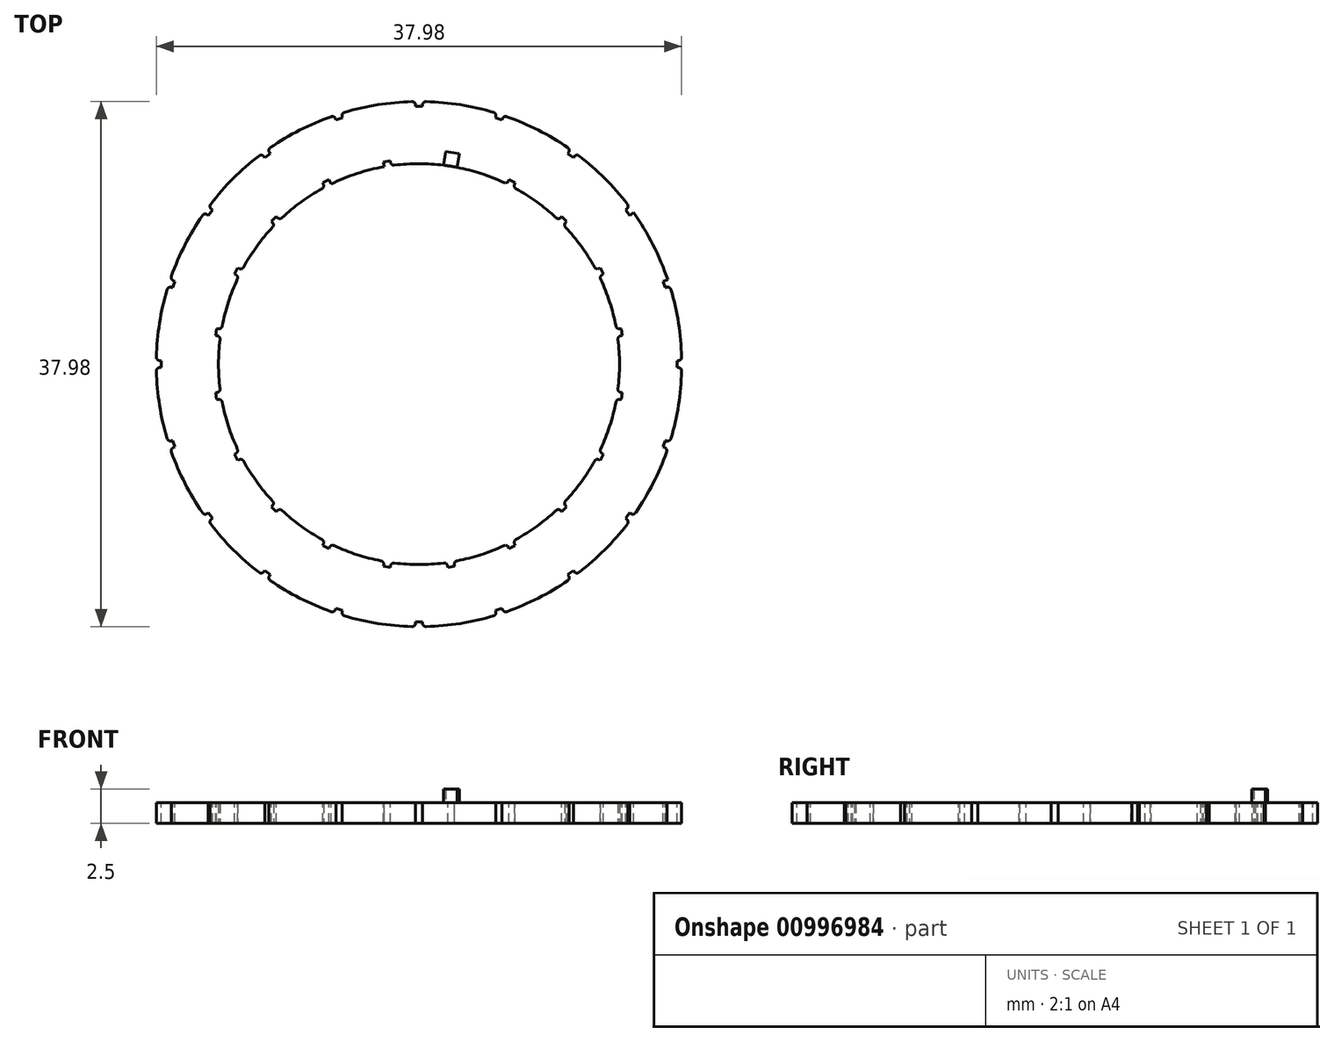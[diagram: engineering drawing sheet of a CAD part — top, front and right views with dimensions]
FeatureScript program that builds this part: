
annotation { "Feature Type Name" : "Feature", "Feature Type Description" : "" }
export const myFeature = defineFeature(function(context is Context, id is Id, definition is map)
    precondition{}
    {
        {
            var Q0;
            Q0=qCreatedBy(makeId("Top.planeOp"),FACE);
            var sketch = newSketch(context, id + "F0", { "sketchPlane" : qUnion([Q0])});
            skCircle(sketch, "E0", {"center": v(0, 0) * mm, "radius": 19 * mm});
            skCircle(sketch, "E1", {"center": v(0, 0) * mm, "radius": 14.5 * mm});
            skSolve(sketch);
        }
        {
            var Q0;
            Q0 = qSketchRegion(id + "F0", true);
            extrude(context, id + "F1", {"entities" : qUnion([Q0]), "depth" : 1.5 * mm, "offsetDistance" : 25 * mm});
        }
        {
            var Q0;
            Q0=makeQuery(id+"F1.opExtrude","CAP_FACE",FACE,{"disambiguationData":[OSD([sQuery(id+"F0.wireOp",EDGE,"E0"),sQuery(id+"F0.wireOp",EDGE,"E1")])],"isStart":false});
            var sketch = newSketch(context, id + "F2", { "sketchPlane" : qUnion([Q0])});
            skLineSegment(sketch, "E2", {"start": v(-0.25, 19) * mm, "end": v(-0.25, 18.65) * mm});
            skLineSegment(sketch, "E3", {"start": v(-0.25, 18.65) * mm, "end": v(0.25, 18.65) * mm});
            skLineSegment(sketch, "E4", {"start": v(0.25, 18.65) * mm, "end": v(0.25, 19) * mm});
            skArc(sketch, "E5", {"start": v(0.25, 19) * mm, "mid": v(0, 19) * mm, "end": v(-0.25, 19) * mm});
            skLineSegment(sketch, "E6.1.0", {"start": v(-6.1, 18) * mm, "end": v(-6, 17.66) * mm});
            skLineSegment(sketch, "E6.1.1", {"start": v(-5.52, 17.81) * mm, "end": v(-5.63, 18.15) * mm});
            skArc(sketch, "E6.1.2", {"start": v(-5.63, 18.15) * mm, "mid": v(-5.87, 18.07) * mm, "end": v(-6.1, 18) * mm});
            skLineSegment(sketch, "E6.1.3", {"start": v(-6, 17.66) * mm, "end": v(-5.52, 17.81) * mm});
            skLineSegment(sketch, "E6.2.0", {"start": v(-11.37, 15.22) * mm, "end": v(-11.16, 14.94) * mm});
            skLineSegment(sketch, "E6.2.1", {"start": v(-10.76, 15.23) * mm, "end": v(-10.96, 15.52) * mm});
            skArc(sketch, "E6.2.2", {"start": v(-10.96, 15.52) * mm, "mid": v(-11.17, 15.37) * mm, "end": v(-11.37, 15.22) * mm});
            skLineSegment(sketch, "E6.2.3", {"start": v(-11.16, 14.94) * mm, "end": v(-10.76, 15.23) * mm});
            skLineSegment(sketch, "E6.3.0", {"start": v(-15.52, 10.96) * mm, "end": v(-15.23, 10.76) * mm});
            skLineSegment(sketch, "E6.3.1", {"start": v(-14.94, 11.16) * mm, "end": v(-15.22, 11.37) * mm});
            skArc(sketch, "E6.3.2", {"start": v(-15.22, 11.37) * mm, "mid": v(-15.37, 11.17) * mm, "end": v(-15.52, 10.96) * mm});
            skLineSegment(sketch, "E6.3.3", {"start": v(-15.23, 10.76) * mm, "end": v(-14.94, 11.16) * mm});
            skLineSegment(sketch, "E6.4.0", {"start": v(-18.15, 5.63) * mm, "end": v(-17.81, 5.52) * mm});
            skLineSegment(sketch, "E6.4.1", {"start": v(-17.66, 6) * mm, "end": v(-18, 6.1) * mm});
            skArc(sketch, "E6.4.2", {"start": v(-18, 6.1) * mm, "mid": v(-18.07, 5.87) * mm, "end": v(-18.15, 5.63) * mm});
            skLineSegment(sketch, "E6.4.3", {"start": v(-17.81, 5.52) * mm, "end": v(-17.66, 6) * mm});
            skLineSegment(sketch, "E6.5.0", {"start": v(-19, -0.25) * mm, "end": v(-18.65, -0.25) * mm});
            skLineSegment(sketch, "E6.5.1", {"start": v(-18.65, 0.25) * mm, "end": v(-19, 0.25) * mm});
            skArc(sketch, "E6.5.2", {"start": v(-19, 0.25) * mm, "mid": v(-19, 0) * mm, "end": v(-19, -0.25) * mm});
            skLineSegment(sketch, "E6.5.3", {"start": v(-18.65, -0.25) * mm, "end": v(-18.65, 0.25) * mm});
            skLineSegment(sketch, "E6.6.0", {"start": v(-18, -6.1) * mm, "end": v(-17.66, -6) * mm});
            skLineSegment(sketch, "E6.6.1", {"start": v(-17.81, -5.52) * mm, "end": v(-18.15, -5.63) * mm});
            skArc(sketch, "E6.6.2", {"start": v(-18.15, -5.63) * mm, "mid": v(-18.07, -5.87) * mm, "end": v(-18, -6.1) * mm});
            skLineSegment(sketch, "E6.6.3", {"start": v(-17.66, -6) * mm, "end": v(-17.81, -5.52) * mm});
            skLineSegment(sketch, "E6.7.0", {"start": v(-15.22, -11.37) * mm, "end": v(-14.94, -11.16) * mm});
            skLineSegment(sketch, "E6.7.1", {"start": v(-15.23, -10.76) * mm, "end": v(-15.52, -10.96) * mm});
            skArc(sketch, "E6.7.2", {"start": v(-15.52, -10.96) * mm, "mid": v(-15.37, -11.17) * mm, "end": v(-15.22, -11.37) * mm});
            skLineSegment(sketch, "E6.7.3", {"start": v(-14.94, -11.16) * mm, "end": v(-15.23, -10.76) * mm});
            skLineSegment(sketch, "E6.8.0", {"start": v(-10.96, -15.52) * mm, "end": v(-10.76, -15.23) * mm});
            skLineSegment(sketch, "E6.8.1", {"start": v(-11.16, -14.94) * mm, "end": v(-11.37, -15.22) * mm});
            skArc(sketch, "E6.8.2", {"start": v(-11.37, -15.22) * mm, "mid": v(-11.17, -15.37) * mm, "end": v(-10.96, -15.52) * mm});
            skLineSegment(sketch, "E6.8.3", {"start": v(-10.76, -15.23) * mm, "end": v(-11.16, -14.94) * mm});
            skLineSegment(sketch, "E6.9.0", {"start": v(-5.63, -18.15) * mm, "end": v(-5.52, -17.81) * mm});
            skLineSegment(sketch, "E6.9.1", {"start": v(-6, -17.66) * mm, "end": v(-6.1, -18) * mm});
            skArc(sketch, "E6.9.2", {"start": v(-6.1, -18) * mm, "mid": v(-5.87, -18.07) * mm, "end": v(-5.63, -18.15) * mm});
            skLineSegment(sketch, "E6.9.3", {"start": v(-5.52, -17.81) * mm, "end": v(-6, -17.66) * mm});
            skLineSegment(sketch, "E6.10.0", {"start": v(0.25, -19) * mm, "end": v(0.25, -18.65) * mm});
            skLineSegment(sketch, "E6.10.1", {"start": v(-0.25, -18.65) * mm, "end": v(-0.25, -19) * mm});
            skArc(sketch, "E6.10.2", {"start": v(-0.25, -19) * mm, "mid": v(0, -19) * mm, "end": v(0.25, -19) * mm});
            skLineSegment(sketch, "E6.10.3", {"start": v(0.25, -18.65) * mm, "end": v(-0.25, -18.65) * mm});
            skLineSegment(sketch, "E6.11.0", {"start": v(6.1, -18) * mm, "end": v(6, -17.66) * mm});
            skLineSegment(sketch, "E6.11.1", {"start": v(5.52, -17.81) * mm, "end": v(5.63, -18.15) * mm});
            skArc(sketch, "E6.11.2", {"start": v(5.63, -18.15) * mm, "mid": v(5.87, -18.07) * mm, "end": v(6.1, -18) * mm});
            skLineSegment(sketch, "E6.11.3", {"start": v(6, -17.66) * mm, "end": v(5.52, -17.81) * mm});
            skLineSegment(sketch, "E6.12.0", {"start": v(11.37, -15.22) * mm, "end": v(11.16, -14.94) * mm});
            skLineSegment(sketch, "E6.12.1", {"start": v(10.76, -15.23) * mm, "end": v(10.96, -15.52) * mm});
            skArc(sketch, "E6.12.2", {"start": v(10.96, -15.52) * mm, "mid": v(11.17, -15.37) * mm, "end": v(11.37, -15.22) * mm});
            skLineSegment(sketch, "E6.12.3", {"start": v(11.16, -14.94) * mm, "end": v(10.76, -15.23) * mm});
            skLineSegment(sketch, "E6.13.0", {"start": v(15.52, -10.96) * mm, "end": v(15.23, -10.76) * mm});
            skLineSegment(sketch, "E6.13.1", {"start": v(14.94, -11.16) * mm, "end": v(15.22, -11.37) * mm});
            skArc(sketch, "E6.13.2", {"start": v(15.22, -11.37) * mm, "mid": v(15.37, -11.17) * mm, "end": v(15.52, -10.96) * mm});
            skLineSegment(sketch, "E6.13.3", {"start": v(15.23, -10.76) * mm, "end": v(14.94, -11.16) * mm});
            skLineSegment(sketch, "E6.14.0", {"start": v(18.15, -5.63) * mm, "end": v(17.81, -5.52) * mm});
            skLineSegment(sketch, "E6.14.1", {"start": v(17.66, -6) * mm, "end": v(18, -6.1) * mm});
            skArc(sketch, "E6.14.2", {"start": v(18, -6.1) * mm, "mid": v(18.07, -5.87) * mm, "end": v(18.15, -5.63) * mm});
            skLineSegment(sketch, "E6.14.3", {"start": v(17.81, -5.52) * mm, "end": v(17.66, -6) * mm});
            skLineSegment(sketch, "E6.15.0", {"start": v(19, 0.25) * mm, "end": v(18.65, 0.25) * mm});
            skLineSegment(sketch, "E6.15.1", {"start": v(18.65, -0.25) * mm, "end": v(19, -0.25) * mm});
            skArc(sketch, "E6.15.2", {"start": v(19, -0.25) * mm, "mid": v(19, 0) * mm, "end": v(19, 0.25) * mm});
            skLineSegment(sketch, "E6.15.3", {"start": v(18.65, 0.25) * mm, "end": v(18.65, -0.25) * mm});
            skLineSegment(sketch, "E6.16.0", {"start": v(18, 6.1) * mm, "end": v(17.66, 6) * mm});
            skLineSegment(sketch, "E6.16.1", {"start": v(17.81, 5.52) * mm, "end": v(18.15, 5.63) * mm});
            skArc(sketch, "E6.16.2", {"start": v(18.15, 5.63) * mm, "mid": v(18.07, 5.87) * mm, "end": v(18, 6.1) * mm});
            skLineSegment(sketch, "E6.16.3", {"start": v(17.66, 6) * mm, "end": v(17.81, 5.52) * mm});
            skLineSegment(sketch, "E6.17.0", {"start": v(15.22, 11.37) * mm, "end": v(14.94, 11.16) * mm});
            skLineSegment(sketch, "E6.17.1", {"start": v(15.23, 10.76) * mm, "end": v(15.52, 10.96) * mm});
            skArc(sketch, "E6.17.2", {"start": v(15.52, 10.96) * mm, "mid": v(15.37, 11.17) * mm, "end": v(15.22, 11.37) * mm});
            skLineSegment(sketch, "E6.17.3", {"start": v(14.94, 11.16) * mm, "end": v(15.23, 10.76) * mm});
            skLineSegment(sketch, "E6.18.0", {"start": v(10.96, 15.52) * mm, "end": v(10.76, 15.23) * mm});
            skLineSegment(sketch, "E6.18.1", {"start": v(11.16, 14.94) * mm, "end": v(11.37, 15.22) * mm});
            skArc(sketch, "E6.18.2", {"start": v(11.37, 15.22) * mm, "mid": v(11.17, 15.37) * mm, "end": v(10.96, 15.52) * mm});
            skLineSegment(sketch, "E6.18.3", {"start": v(10.76, 15.23) * mm, "end": v(11.16, 14.94) * mm});
            skLineSegment(sketch, "E6.19.0", {"start": v(5.63, 18.15) * mm, "end": v(5.52, 17.81) * mm});
            skLineSegment(sketch, "E6.19.1", {"start": v(6, 17.66) * mm, "end": v(6.1, 18) * mm});
            skArc(sketch, "E6.19.2", {"start": v(6.1, 18) * mm, "mid": v(5.87, 18.07) * mm, "end": v(5.63, 18.15) * mm});
            skLineSegment(sketch, "E6.19.3", {"start": v(5.52, 17.81) * mm, "end": v(6, 17.66) * mm});
            skSolve(sketch);
        }
        {
            var Q0;
            Q0 = qSketchRegion(id + "F2", true);
            extrude(context, id + "F3", {"entities" : qUnion([Q0]), "operationType" : NewBodyOperationType.REMOVE, "endBound" : BoundingType.THROUGH_ALL, "oppositeDirection" : true, "depth" : 25 * mm, "offsetDistance" : 25 * mm});
        }
        {
            var Q0;
            Q0=makeQuery(id+"F1.opExtrude","CAP_FACE",FACE,{"disambiguationData":[OSD([sQuery(id+"F0.wireOp",EDGE,"E0"),sQuery(id+"F0.wireOp",EDGE,"E1")])],"isStart":false});
            var sketch = newSketch(context, id + "F4", { "sketchPlane" : qUnion([Q0])});
            skLineSegment(sketch, "E7", {"start": v(0, 0) * mm, "end": v(-2.5, 15.78) * mm, "construction": true});
            skLineSegment(sketch, "E8", {"start": v(-2.51, 14.28) * mm, "end": v(-2.57, 14.63) * mm});
            skLineSegment(sketch, "E9", {"start": v(-2.57, 14.63) * mm, "end": v(-2.08, 14.7) * mm});
            skLineSegment(sketch, "E10", {"start": v(-2.08, 14.7) * mm, "end": v(-2.02, 14.36) * mm});
            skArc(sketch, "E11", {"start": v(-2.02, 14.36) * mm, "mid": v(-2.27, 14.32) * mm, "end": v(-2.51, 14.28) * mm});
            skLineSegment(sketch, "E12.1.0", {"start": v(-6.8, 12.8) * mm, "end": v(-6.96, 13.12) * mm});
            skLineSegment(sketch, "E12.1.1", {"start": v(-6.52, 13.34) * mm, "end": v(-6.36, 13.03) * mm});
            skLineSegment(sketch, "E12.1.2", {"start": v(-6.96, 13.12) * mm, "end": v(-6.52, 13.34) * mm});
            skArc(sketch, "E12.1.3", {"start": v(-6.36, 13.03) * mm, "mid": v(-6.58, 12.92) * mm, "end": v(-6.8, 12.8) * mm});
            skLineSegment(sketch, "E12.2.0", {"start": v(-10.43, 10.07) * mm, "end": v(-10.68, 10.32) * mm});
            skLineSegment(sketch, "E12.2.1", {"start": v(-10.32, 10.68) * mm, "end": v(-10.07, 10.43) * mm});
            skLineSegment(sketch, "E12.2.2", {"start": v(-10.68, 10.32) * mm, "end": v(-10.32, 10.68) * mm});
            skArc(sketch, "E12.2.3", {"start": v(-10.07, 10.43) * mm, "mid": v(-10.25, 10.25) * mm, "end": v(-10.43, 10.07) * mm});
            skLineSegment(sketch, "E12.3.0", {"start": v(-13.03, 6.36) * mm, "end": v(-13.34, 6.52) * mm});
            skLineSegment(sketch, "E12.3.1", {"start": v(-13.12, 6.96) * mm, "end": v(-12.8, 6.8) * mm});
            skLineSegment(sketch, "E12.3.2", {"start": v(-13.34, 6.52) * mm, "end": v(-13.12, 6.96) * mm});
            skArc(sketch, "E12.3.3", {"start": v(-12.8, 6.8) * mm, "mid": v(-12.92, 6.58) * mm, "end": v(-13.03, 6.36) * mm});
            skLineSegment(sketch, "E12.4.0", {"start": v(-14.36, 2.02) * mm, "end": v(-14.7, 2.08) * mm});
            skLineSegment(sketch, "E12.4.1", {"start": v(-14.63, 2.57) * mm, "end": v(-14.28, 2.51) * mm});
            skLineSegment(sketch, "E12.4.2", {"start": v(-14.7, 2.08) * mm, "end": v(-14.63, 2.57) * mm});
            skArc(sketch, "E12.4.3", {"start": v(-14.28, 2.51) * mm, "mid": v(-14.32, 2.27) * mm, "end": v(-14.36, 2.02) * mm});
            skLineSegment(sketch, "E12.5.0", {"start": v(-14.28, -2.51) * mm, "end": v(-14.63, -2.57) * mm});
            skLineSegment(sketch, "E12.5.1", {"start": v(-14.7, -2.08) * mm, "end": v(-14.36, -2.02) * mm});
            skLineSegment(sketch, "E12.5.2", {"start": v(-14.63, -2.57) * mm, "end": v(-14.7, -2.08) * mm});
            skArc(sketch, "E12.5.3", {"start": v(-14.36, -2.02) * mm, "mid": v(-14.32, -2.27) * mm, "end": v(-14.28, -2.51) * mm});
            skLineSegment(sketch, "E12.6.0", {"start": v(-12.8, -6.8) * mm, "end": v(-13.12, -6.96) * mm});
            skLineSegment(sketch, "E12.6.1", {"start": v(-13.34, -6.52) * mm, "end": v(-13.03, -6.36) * mm});
            skLineSegment(sketch, "E12.6.2", {"start": v(-13.12, -6.96) * mm, "end": v(-13.34, -6.52) * mm});
            skArc(sketch, "E12.6.3", {"start": v(-13.03, -6.36) * mm, "mid": v(-12.92, -6.58) * mm, "end": v(-12.8, -6.8) * mm});
            skLineSegment(sketch, "E12.7.0", {"start": v(-10.07, -10.43) * mm, "end": v(-10.32, -10.68) * mm});
            skLineSegment(sketch, "E12.7.1", {"start": v(-10.68, -10.32) * mm, "end": v(-10.43, -10.07) * mm});
            skLineSegment(sketch, "E12.7.2", {"start": v(-10.32, -10.68) * mm, "end": v(-10.68, -10.32) * mm});
            skArc(sketch, "E12.7.3", {"start": v(-10.43, -10.07) * mm, "mid": v(-10.25, -10.25) * mm, "end": v(-10.07, -10.43) * mm});
            skLineSegment(sketch, "E12.8.0", {"start": v(-6.36, -13.03) * mm, "end": v(-6.52, -13.34) * mm});
            skLineSegment(sketch, "E12.8.1", {"start": v(-6.96, -13.12) * mm, "end": v(-6.8, -12.8) * mm});
            skLineSegment(sketch, "E12.8.2", {"start": v(-6.52, -13.34) * mm, "end": v(-6.96, -13.12) * mm});
            skArc(sketch, "E12.8.3", {"start": v(-6.8, -12.8) * mm, "mid": v(-6.58, -12.92) * mm, "end": v(-6.36, -13.03) * mm});
            skLineSegment(sketch, "E12.9.0", {"start": v(-2.02, -14.36) * mm, "end": v(-2.08, -14.7) * mm});
            skLineSegment(sketch, "E12.9.1", {"start": v(-2.57, -14.63) * mm, "end": v(-2.51, -14.28) * mm});
            skLineSegment(sketch, "E12.9.2", {"start": v(-2.08, -14.7) * mm, "end": v(-2.57, -14.63) * mm});
            skArc(sketch, "E12.9.3", {"start": v(-2.51, -14.28) * mm, "mid": v(-2.27, -14.32) * mm, "end": v(-2.02, -14.36) * mm});
            skLineSegment(sketch, "E12.10.0", {"start": v(2.51, -14.28) * mm, "end": v(2.57, -14.63) * mm});
            skLineSegment(sketch, "E12.10.1", {"start": v(2.08, -14.7) * mm, "end": v(2.02, -14.36) * mm});
            skLineSegment(sketch, "E12.10.2", {"start": v(2.57, -14.63) * mm, "end": v(2.08, -14.7) * mm});
            skArc(sketch, "E12.10.3", {"start": v(2.02, -14.36) * mm, "mid": v(2.27, -14.32) * mm, "end": v(2.51, -14.28) * mm});
            skLineSegment(sketch, "E12.11.0", {"start": v(6.8, -12.8) * mm, "end": v(6.96, -13.12) * mm});
            skLineSegment(sketch, "E12.11.1", {"start": v(6.52, -13.34) * mm, "end": v(6.36, -13.03) * mm});
            skLineSegment(sketch, "E12.11.2", {"start": v(6.96, -13.12) * mm, "end": v(6.52, -13.34) * mm});
            skArc(sketch, "E12.11.3", {"start": v(6.36, -13.03) * mm, "mid": v(6.58, -12.92) * mm, "end": v(6.8, -12.8) * mm});
            skLineSegment(sketch, "E12.12.0", {"start": v(10.43, -10.07) * mm, "end": v(10.68, -10.32) * mm});
            skLineSegment(sketch, "E12.12.1", {"start": v(10.32, -10.68) * mm, "end": v(10.07, -10.43) * mm});
            skLineSegment(sketch, "E12.12.2", {"start": v(10.68, -10.32) * mm, "end": v(10.32, -10.68) * mm});
            skArc(sketch, "E12.12.3", {"start": v(10.07, -10.43) * mm, "mid": v(10.25, -10.25) * mm, "end": v(10.43, -10.07) * mm});
            skLineSegment(sketch, "E12.13.0", {"start": v(13.03, -6.36) * mm, "end": v(13.34, -6.52) * mm});
            skLineSegment(sketch, "E12.13.1", {"start": v(13.12, -6.96) * mm, "end": v(12.8, -6.8) * mm});
            skLineSegment(sketch, "E12.13.2", {"start": v(13.34, -6.52) * mm, "end": v(13.12, -6.96) * mm});
            skArc(sketch, "E12.13.3", {"start": v(12.8, -6.8) * mm, "mid": v(12.92, -6.58) * mm, "end": v(13.03, -6.36) * mm});
            skLineSegment(sketch, "E12.14.0", {"start": v(14.36, -2.02) * mm, "end": v(14.7, -2.08) * mm});
            skLineSegment(sketch, "E12.14.1", {"start": v(14.63, -2.57) * mm, "end": v(14.28, -2.51) * mm});
            skLineSegment(sketch, "E12.14.2", {"start": v(14.7, -2.08) * mm, "end": v(14.63, -2.57) * mm});
            skArc(sketch, "E12.14.3", {"start": v(14.28, -2.51) * mm, "mid": v(14.32, -2.27) * mm, "end": v(14.36, -2.02) * mm});
            skLineSegment(sketch, "E12.15.0", {"start": v(14.28, 2.51) * mm, "end": v(14.63, 2.57) * mm});
            skLineSegment(sketch, "E12.15.1", {"start": v(14.7, 2.08) * mm, "end": v(14.36, 2.02) * mm});
            skLineSegment(sketch, "E12.15.2", {"start": v(14.63, 2.57) * mm, "end": v(14.7, 2.08) * mm});
            skArc(sketch, "E12.15.3", {"start": v(14.36, 2.02) * mm, "mid": v(14.32, 2.27) * mm, "end": v(14.28, 2.51) * mm});
            skLineSegment(sketch, "E12.16.0", {"start": v(12.8, 6.8) * mm, "end": v(13.12, 6.96) * mm});
            skLineSegment(sketch, "E12.16.1", {"start": v(13.34, 6.52) * mm, "end": v(13.03, 6.36) * mm});
            skLineSegment(sketch, "E12.16.2", {"start": v(13.12, 6.96) * mm, "end": v(13.34, 6.52) * mm});
            skArc(sketch, "E12.16.3", {"start": v(13.03, 6.36) * mm, "mid": v(12.92, 6.58) * mm, "end": v(12.8, 6.8) * mm});
            skLineSegment(sketch, "E12.17.0", {"start": v(10.07, 10.43) * mm, "end": v(10.32, 10.68) * mm});
            skLineSegment(sketch, "E12.17.1", {"start": v(10.68, 10.32) * mm, "end": v(10.43, 10.07) * mm});
            skLineSegment(sketch, "E12.17.2", {"start": v(10.32, 10.68) * mm, "end": v(10.68, 10.32) * mm});
            skArc(sketch, "E12.17.3", {"start": v(10.43, 10.07) * mm, "mid": v(10.25, 10.25) * mm, "end": v(10.07, 10.43) * mm});
            skLineSegment(sketch, "E12.18.0", {"start": v(6.36, 13.03) * mm, "end": v(6.52, 13.34) * mm});
            skLineSegment(sketch, "E12.18.1", {"start": v(6.96, 13.12) * mm, "end": v(6.8, 12.8) * mm});
            skLineSegment(sketch, "E12.18.2", {"start": v(6.52, 13.34) * mm, "end": v(6.96, 13.12) * mm});
            skArc(sketch, "E12.18.3", {"start": v(6.8, 12.8) * mm, "mid": v(6.58, 12.92) * mm, "end": v(6.36, 13.03) * mm});
            skLineSegment(sketch, "E12.19.0", {"start": v(2.02, 14.36) * mm, "end": v(2.08, 14.7) * mm});
            skLineSegment(sketch, "E12.19.1", {"start": v(2.57, 14.63) * mm, "end": v(2.51, 14.28) * mm});
            skLineSegment(sketch, "E12.19.2", {"start": v(2.08, 14.7) * mm, "end": v(2.57, 14.63) * mm});
            skArc(sketch, "E12.19.3", {"start": v(2.51, 14.28) * mm, "mid": v(2.27, 14.32) * mm, "end": v(2.02, 14.36) * mm});
            skSolve(sketch);
        }
        {
            var Q0;
            Q0 = qSketchRegion(id + "F4", true);
            extrude(context, id + "F5", {"entities" : qUnion([Q0]), "operationType" : NewBodyOperationType.REMOVE, "endBound" : BoundingType.THROUGH_ALL, "oppositeDirection" : true, "depth" : 25 * mm, "offsetDistance" : 25 * mm});
        }
        {
            var Q0;
            Q0=makeQuery(id+"F1.opExtrude","CAP_FACE",FACE,{"disambiguationData":[OSD([sQuery(id+"F0.wireOp",EDGE,"E0"),sQuery(id+"F0.wireOp",EDGE,"E1")])],"isStart":true});
            var sketch = newSketch(context, id + "F6", { "sketchPlane" : qUnion([Q0])});
            skLineSegment(sketch, "E13", {"start": v(2.51, -14.28) * mm, "end": v(2.57, -14.63) * mm});
            skLineSegment(sketch, "E14", {"start": v(2.57, -14.63) * mm, "end": v(2.08, -14.7) * mm});
            skLineSegment(sketch, "E15", {"start": v(2.08, -14.7) * mm, "end": v(2.02, -14.36) * mm});
            skArc(sketch, "E16", {"start": v(2.02, -14.36) * mm, "mid": v(2.27, -14.32) * mm, "end": v(2.51, -14.28) * mm});
            skSolve(sketch);
        }
        {
            var Q0;
            Q0 = qSketchRegion(id + "F6", true);
            extrude(context, id + "F7", {"entities" : qUnion([Q0]), "operationType" : NewBodyOperationType.ADD, "oppositeDirection" : true, "depth" : 2.5 * mm, "offsetDistance" : 25 * mm});
        }
        {
            var Q0;
            Q0=makeQuery(id+"F1.opExtrude","CAP_FACE",FACE,{"disambiguationData":[OSD([sQuery(id+"F0.wireOp",EDGE,"E0"),sQuery(id+"F0.wireOp",EDGE,"E1")])],"isStart":false});
            var sketch = newSketch(context, id + "F8", { "sketchPlane" : qUnion([Q0])});
            skLineSegment(sketch, "E17", {"start": v(1.77, 14.4) * mm, "end": v(1.93, 15.38) * mm});
            skLineSegment(sketch, "E18", {"start": v(1.93, 15.38) * mm, "end": v(2.92, 15.22) * mm});
            skLineSegment(sketch, "E19", {"start": v(2.92, 15.22) * mm, "end": v(2.76, 14.23) * mm});
            skArc(sketch, "E20", {"start": v(2.76, 14.23) * mm, "mid": v(2.27, 14.32) * mm, "end": v(1.77, 14.4) * mm});
            skSolve(sketch);
        }
        {
            var Q0;
            Q0 = qSketchRegion(id + "F8", true);
            var Q1;
            Q1=makeQuery(id+"F7.opExtrude","CAP_FACE",FACE,{"disambiguationData":[OSD([sQuery(id+"F6.wireOp",EDGE,"E13"),sQuery(id+"F6.wireOp",EDGE,"E14"),sQuery(id+"F6.wireOp",EDGE,"E15"),sQuery(id+"F6.wireOp",EDGE,"E16")])],"isStart":false});
            extrude(context, id + "F9", {"entities" : qUnion([Q0]), "operationType" : NewBodyOperationType.ADD, "endBound" : BoundingType.UP_TO_SURFACE, "depth" : 25 * mm, "endBoundEntityFace" : qUnion([Q1]), "offsetDistance" : 25 * mm});
        }
        {
            var Q0;
            Q0=makeQuery(id+"F3.boolean.opBoolean","COPY",EDGE,{"derivedFrom":makeQuery(id+"F3.opExtrude","SWEPT_EDGE",EDGE,{"disambiguationData":[OSD([sQuery(id+"F0.wireOp",EDGE,"E0"),sQuery(id+"F2.wireOp",EDGE,"E6.19.1"),sQuery(id+"F2.wireOp",EDGE,"E6.19.2")])]})});
            var Q1;
            Q1=makeQuery(id+"F3.boolean.opBoolean","COPY",EDGE,{"derivedFrom":makeQuery(id+"F3.opExtrude","SWEPT_EDGE",EDGE,{"disambiguationData":[OSD([sQuery(id+"F0.wireOp",EDGE,"E0"),sQuery(id+"F2.wireOp",EDGE,"E6.19.0"),sQuery(id+"F2.wireOp",EDGE,"E6.19.2")])]})});
            var Q2;
            Q2=makeQuery(id+"F3.boolean.opBoolean","COPY",EDGE,{"derivedFrom":makeQuery(id+"F3.opExtrude","SWEPT_EDGE",EDGE,{"disambiguationData":[OSD([sQuery(id+"F0.wireOp",EDGE,"E0"),sQuery(id+"F2.wireOp",EDGE,"E4"),sQuery(id+"F2.wireOp",EDGE,"E5")])]})});
            var Q3;
            Q3=makeQuery(id+"F3.boolean.opBoolean","COPY",EDGE,{"derivedFrom":makeQuery(id+"F3.opExtrude","SWEPT_EDGE",EDGE,{"disambiguationData":[OSD([sQuery(id+"F0.wireOp",EDGE,"E0"),sQuery(id+"F2.wireOp",EDGE,"E2"),sQuery(id+"F2.wireOp",EDGE,"E5")])]})});
            var Q4;
            Q4=makeQuery(id+"F3.boolean.opBoolean","COPY",EDGE,{"derivedFrom":makeQuery(id+"F3.opExtrude","SWEPT_EDGE",EDGE,{"disambiguationData":[OSD([sQuery(id+"F0.wireOp",EDGE,"E0"),sQuery(id+"F2.wireOp",EDGE,"E6.1.1"),sQuery(id+"F2.wireOp",EDGE,"E6.1.2")])]})});
            var Q5;
            Q5=makeQuery(id+"F3.boolean.opBoolean","COPY",EDGE,{"derivedFrom":makeQuery(id+"F3.opExtrude","SWEPT_EDGE",EDGE,{"disambiguationData":[OSD([sQuery(id+"F0.wireOp",EDGE,"E0"),sQuery(id+"F2.wireOp",EDGE,"E6.1.0"),sQuery(id+"F2.wireOp",EDGE,"E6.1.2")])]})});
            var Q6;
            Q6=makeQuery(id+"F3.boolean.opBoolean","COPY",EDGE,{"derivedFrom":makeQuery(id+"F3.opExtrude","SWEPT_EDGE",EDGE,{"disambiguationData":[OSD([sQuery(id+"F0.wireOp",EDGE,"E0"),sQuery(id+"F2.wireOp",EDGE,"E6.18.0"),sQuery(id+"F2.wireOp",EDGE,"E6.18.2")])]})});
            var Q7;
            Q7=makeQuery(id+"F3.boolean.opBoolean","COPY",EDGE,{"derivedFrom":makeQuery(id+"F3.opExtrude","SWEPT_EDGE",EDGE,{"disambiguationData":[OSD([sQuery(id+"F0.wireOp",EDGE,"E0"),sQuery(id+"F2.wireOp",EDGE,"E6.18.1"),sQuery(id+"F2.wireOp",EDGE,"E6.18.2")])]})});
            var Q8;
            Q8=makeQuery(id+"F3.boolean.opBoolean","COPY",EDGE,{"derivedFrom":makeQuery(id+"F3.opExtrude","SWEPT_EDGE",EDGE,{"disambiguationData":[OSD([sQuery(id+"F0.wireOp",EDGE,"E0"),sQuery(id+"F2.wireOp",EDGE,"E6.17.0"),sQuery(id+"F2.wireOp",EDGE,"E6.17.2")])]})});
            var Q9;
            Q9=makeQuery(id+"F3.boolean.opBoolean","COPY",EDGE,{"derivedFrom":makeQuery(id+"F3.opExtrude","SWEPT_EDGE",EDGE,{"disambiguationData":[OSD([sQuery(id+"F0.wireOp",EDGE,"E0"),sQuery(id+"F2.wireOp",EDGE,"E6.17.1"),sQuery(id+"F2.wireOp",EDGE,"E6.17.2")])]})});
            var Q10;
            Q10=makeQuery(id+"F3.boolean.opBoolean","COPY",EDGE,{"derivedFrom":makeQuery(id+"F3.opExtrude","SWEPT_EDGE",EDGE,{"disambiguationData":[OSD([sQuery(id+"F0.wireOp",EDGE,"E0"),sQuery(id+"F2.wireOp",EDGE,"E6.16.0"),sQuery(id+"F2.wireOp",EDGE,"E6.16.2")])]})});
            var Q11;
            Q11=makeQuery(id+"F3.boolean.opBoolean","COPY",EDGE,{"derivedFrom":makeQuery(id+"F3.opExtrude","SWEPT_EDGE",EDGE,{"disambiguationData":[OSD([sQuery(id+"F0.wireOp",EDGE,"E0"),sQuery(id+"F2.wireOp",EDGE,"E6.16.1"),sQuery(id+"F2.wireOp",EDGE,"E6.16.2")])]})});
            var Q12;
            Q12=makeQuery(id+"F3.boolean.opBoolean","COPY",EDGE,{"derivedFrom":makeQuery(id+"F3.opExtrude","SWEPT_EDGE",EDGE,{"disambiguationData":[OSD([sQuery(id+"F0.wireOp",EDGE,"E0"),sQuery(id+"F2.wireOp",EDGE,"E6.15.0"),sQuery(id+"F2.wireOp",EDGE,"E6.15.2")])]})});
            var Q13;
            Q13=makeQuery(id+"F3.boolean.opBoolean","COPY",EDGE,{"derivedFrom":makeQuery(id+"F3.opExtrude","SWEPT_EDGE",EDGE,{"disambiguationData":[OSD([sQuery(id+"F0.wireOp",EDGE,"E0"),sQuery(id+"F2.wireOp",EDGE,"E6.15.1"),sQuery(id+"F2.wireOp",EDGE,"E6.15.2")])]})});
            var Q14;
            Q14=makeQuery(id+"F3.boolean.opBoolean","COPY",EDGE,{"derivedFrom":makeQuery(id+"F3.opExtrude","SWEPT_EDGE",EDGE,{"disambiguationData":[OSD([sQuery(id+"F0.wireOp",EDGE,"E0"),sQuery(id+"F2.wireOp",EDGE,"E6.14.0"),sQuery(id+"F2.wireOp",EDGE,"E6.14.2")])]})});
            var Q15;
            Q15=makeQuery(id+"F3.boolean.opBoolean","COPY",EDGE,{"derivedFrom":makeQuery(id+"F3.opExtrude","SWEPT_EDGE",EDGE,{"disambiguationData":[OSD([sQuery(id+"F0.wireOp",EDGE,"E0"),sQuery(id+"F2.wireOp",EDGE,"E6.14.1"),sQuery(id+"F2.wireOp",EDGE,"E6.14.2")])]})});
            var Q16;
            Q16=makeQuery(id+"F3.boolean.opBoolean","COPY",EDGE,{"derivedFrom":makeQuery(id+"F3.opExtrude","SWEPT_EDGE",EDGE,{"disambiguationData":[OSD([sQuery(id+"F0.wireOp",EDGE,"E0"),sQuery(id+"F2.wireOp",EDGE,"E6.13.0"),sQuery(id+"F2.wireOp",EDGE,"E6.13.2")])]})});
            var Q17;
            Q17=makeQuery(id+"F3.boolean.opBoolean","COPY",EDGE,{"derivedFrom":makeQuery(id+"F3.opExtrude","SWEPT_EDGE",EDGE,{"disambiguationData":[OSD([sQuery(id+"F0.wireOp",EDGE,"E0"),sQuery(id+"F2.wireOp",EDGE,"E6.13.1"),sQuery(id+"F2.wireOp",EDGE,"E6.13.2")])]})});
            var Q18;
            Q18=makeQuery(id+"F3.boolean.opBoolean","COPY",EDGE,{"derivedFrom":makeQuery(id+"F3.opExtrude","SWEPT_EDGE",EDGE,{"disambiguationData":[OSD([sQuery(id+"F0.wireOp",EDGE,"E0"),sQuery(id+"F2.wireOp",EDGE,"E6.12.0"),sQuery(id+"F2.wireOp",EDGE,"E6.12.2")])]})});
            var Q19;
            Q19=makeQuery(id+"F3.boolean.opBoolean","COPY",EDGE,{"derivedFrom":makeQuery(id+"F3.opExtrude","SWEPT_EDGE",EDGE,{"disambiguationData":[OSD([sQuery(id+"F0.wireOp",EDGE,"E0"),sQuery(id+"F2.wireOp",EDGE,"E6.12.1"),sQuery(id+"F2.wireOp",EDGE,"E6.12.2")])]})});
            var Q20;
            Q20=makeQuery(id+"F3.boolean.opBoolean","COPY",EDGE,{"derivedFrom":makeQuery(id+"F3.opExtrude","SWEPT_EDGE",EDGE,{"disambiguationData":[OSD([sQuery(id+"F0.wireOp",EDGE,"E0"),sQuery(id+"F2.wireOp",EDGE,"E6.11.0"),sQuery(id+"F2.wireOp",EDGE,"E6.11.2")])]})});
            var Q21;
            Q21=makeQuery(id+"F3.boolean.opBoolean","COPY",EDGE,{"derivedFrom":makeQuery(id+"F3.opExtrude","SWEPT_EDGE",EDGE,{"disambiguationData":[OSD([sQuery(id+"F0.wireOp",EDGE,"E0"),sQuery(id+"F2.wireOp",EDGE,"E6.11.1"),sQuery(id+"F2.wireOp",EDGE,"E6.11.2")])]})});
            var Q22;
            Q22=makeQuery(id+"F3.boolean.opBoolean","COPY",EDGE,{"derivedFrom":makeQuery(id+"F3.opExtrude","SWEPT_EDGE",EDGE,{"disambiguationData":[OSD([sQuery(id+"F0.wireOp",EDGE,"E0"),sQuery(id+"F2.wireOp",EDGE,"E6.10.0"),sQuery(id+"F2.wireOp",EDGE,"E6.10.2")])]})});
            var Q23;
            Q23=makeQuery(id+"F3.boolean.opBoolean","COPY",EDGE,{"derivedFrom":makeQuery(id+"F3.opExtrude","SWEPT_EDGE",EDGE,{"disambiguationData":[OSD([sQuery(id+"F0.wireOp",EDGE,"E0"),sQuery(id+"F2.wireOp",EDGE,"E6.10.1"),sQuery(id+"F2.wireOp",EDGE,"E6.10.2")])]})});
            var Q24;
            Q24=makeQuery(id+"F3.boolean.opBoolean","COPY",EDGE,{"derivedFrom":makeQuery(id+"F3.opExtrude","SWEPT_EDGE",EDGE,{"disambiguationData":[OSD([sQuery(id+"F0.wireOp",EDGE,"E0"),sQuery(id+"F2.wireOp",EDGE,"E6.9.0"),sQuery(id+"F2.wireOp",EDGE,"E6.9.2")])]})});
            var Q25;
            Q25=makeQuery(id+"F3.boolean.opBoolean","COPY",EDGE,{"derivedFrom":makeQuery(id+"F3.opExtrude","SWEPT_EDGE",EDGE,{"disambiguationData":[OSD([sQuery(id+"F0.wireOp",EDGE,"E0"),sQuery(id+"F2.wireOp",EDGE,"E6.9.1"),sQuery(id+"F2.wireOp",EDGE,"E6.9.2")])]})});
            var Q26;
            Q26=makeQuery(id+"F3.boolean.opBoolean","COPY",EDGE,{"derivedFrom":makeQuery(id+"F3.opExtrude","SWEPT_EDGE",EDGE,{"disambiguationData":[OSD([sQuery(id+"F0.wireOp",EDGE,"E0"),sQuery(id+"F2.wireOp",EDGE,"E6.8.0"),sQuery(id+"F2.wireOp",EDGE,"E6.8.2")])]})});
            var Q27;
            Q27=makeQuery(id+"F3.boolean.opBoolean","COPY",EDGE,{"derivedFrom":makeQuery(id+"F3.opExtrude","SWEPT_EDGE",EDGE,{"disambiguationData":[OSD([sQuery(id+"F0.wireOp",EDGE,"E0"),sQuery(id+"F2.wireOp",EDGE,"E6.8.1"),sQuery(id+"F2.wireOp",EDGE,"E6.8.2")])]})});
            var Q28;
            Q28=makeQuery(id+"F3.boolean.opBoolean","COPY",EDGE,{"derivedFrom":makeQuery(id+"F3.opExtrude","SWEPT_EDGE",EDGE,{"disambiguationData":[OSD([sQuery(id+"F0.wireOp",EDGE,"E0"),sQuery(id+"F2.wireOp",EDGE,"E6.7.0"),sQuery(id+"F2.wireOp",EDGE,"E6.7.2")])]})});
            var Q29;
            Q29=makeQuery(id+"F3.boolean.opBoolean","COPY",EDGE,{"derivedFrom":makeQuery(id+"F3.opExtrude","SWEPT_EDGE",EDGE,{"disambiguationData":[OSD([sQuery(id+"F0.wireOp",EDGE,"E0"),sQuery(id+"F2.wireOp",EDGE,"E6.7.1"),sQuery(id+"F2.wireOp",EDGE,"E6.7.2")])]})});
            var Q30;
            Q30=makeQuery(id+"F3.boolean.opBoolean","COPY",EDGE,{"derivedFrom":makeQuery(id+"F3.opExtrude","SWEPT_EDGE",EDGE,{"disambiguationData":[OSD([sQuery(id+"F0.wireOp",EDGE,"E0"),sQuery(id+"F2.wireOp",EDGE,"E6.6.0"),sQuery(id+"F2.wireOp",EDGE,"E6.6.2")])]})});
            var Q31;
            Q31=makeQuery(id+"F3.boolean.opBoolean","COPY",EDGE,{"derivedFrom":makeQuery(id+"F3.opExtrude","SWEPT_EDGE",EDGE,{"disambiguationData":[OSD([sQuery(id+"F0.wireOp",EDGE,"E0"),sQuery(id+"F2.wireOp",EDGE,"E6.6.1"),sQuery(id+"F2.wireOp",EDGE,"E6.6.2")])]})});
            var Q32;
            Q32=makeQuery(id+"F3.boolean.opBoolean","COPY",EDGE,{"derivedFrom":makeQuery(id+"F3.opExtrude","SWEPT_EDGE",EDGE,{"disambiguationData":[OSD([sQuery(id+"F0.wireOp",EDGE,"E0"),sQuery(id+"F2.wireOp",EDGE,"E6.5.0"),sQuery(id+"F2.wireOp",EDGE,"E6.5.2")])]})});
            var Q33;
            Q33=makeQuery(id+"F3.boolean.opBoolean","COPY",EDGE,{"derivedFrom":makeQuery(id+"F3.opExtrude","SWEPT_EDGE",EDGE,{"disambiguationData":[OSD([sQuery(id+"F0.wireOp",EDGE,"E0"),sQuery(id+"F2.wireOp",EDGE,"E6.5.1"),sQuery(id+"F2.wireOp",EDGE,"E6.5.2")])]})});
            var Q34;
            Q34=makeQuery(id+"F3.boolean.opBoolean","COPY",EDGE,{"derivedFrom":makeQuery(id+"F3.opExtrude","SWEPT_EDGE",EDGE,{"disambiguationData":[OSD([sQuery(id+"F0.wireOp",EDGE,"E0"),sQuery(id+"F2.wireOp",EDGE,"E6.4.0"),sQuery(id+"F2.wireOp",EDGE,"E6.4.2")])]})});
            var Q35;
            Q35=makeQuery(id+"F3.boolean.opBoolean","COPY",EDGE,{"derivedFrom":makeQuery(id+"F3.opExtrude","SWEPT_EDGE",EDGE,{"disambiguationData":[OSD([sQuery(id+"F0.wireOp",EDGE,"E0"),sQuery(id+"F2.wireOp",EDGE,"E6.4.1"),sQuery(id+"F2.wireOp",EDGE,"E6.4.2")])]})});
            var Q36;
            Q36=makeQuery(id+"F3.boolean.opBoolean","COPY",EDGE,{"derivedFrom":makeQuery(id+"F3.opExtrude","SWEPT_EDGE",EDGE,{"disambiguationData":[OSD([sQuery(id+"F0.wireOp",EDGE,"E0"),sQuery(id+"F2.wireOp",EDGE,"E6.3.0"),sQuery(id+"F2.wireOp",EDGE,"E6.3.2")])]})});
            var Q37;
            Q37=makeQuery(id+"F3.boolean.opBoolean","COPY",EDGE,{"derivedFrom":makeQuery(id+"F3.opExtrude","SWEPT_EDGE",EDGE,{"disambiguationData":[OSD([sQuery(id+"F0.wireOp",EDGE,"E0"),sQuery(id+"F2.wireOp",EDGE,"E6.3.1"),sQuery(id+"F2.wireOp",EDGE,"E6.3.2")])]})});
            var Q38;
            Q38=makeQuery(id+"F3.boolean.opBoolean","COPY",EDGE,{"derivedFrom":makeQuery(id+"F3.opExtrude","SWEPT_EDGE",EDGE,{"disambiguationData":[OSD([sQuery(id+"F0.wireOp",EDGE,"E0"),sQuery(id+"F2.wireOp",EDGE,"E6.2.0"),sQuery(id+"F2.wireOp",EDGE,"E6.2.2")])]})});
            var Q39;
            Q39=makeQuery(id+"F3.boolean.opBoolean","COPY",EDGE,{"derivedFrom":makeQuery(id+"F3.opExtrude","SWEPT_EDGE",EDGE,{"disambiguationData":[OSD([sQuery(id+"F0.wireOp",EDGE,"E0"),sQuery(id+"F2.wireOp",EDGE,"E6.2.1"),sQuery(id+"F2.wireOp",EDGE,"E6.2.2")])]})});
            fillet(context, id + "F10", {"entities" : qUnion([Q0, Q1, Q2, Q3, Q4, Q5, Q6, Q7, Q8, Q9, Q10, Q11, Q12, Q13, Q14, Q15, Q16, Q17, Q18, Q19, Q20, Q21, Q22, Q23, Q24, Q25, Q26, Q27, Q28, Q29, Q30, Q31, Q32, Q33, Q34, Q35, Q36, Q37, Q38, Q39]), "radius" : .25 * mm, "tangentPropagation" : true, "allowEdgeOverflow" : false});
        }
        {
            var Q0;
            Q0=makeQuery(id+"F5.boolean.opBoolean","COPY",EDGE,{"derivedFrom":makeQuery(id+"F5.opExtrude","SWEPT_EDGE",EDGE,{"disambiguationData":[OSD([sQuery(id+"F0.wireOp",EDGE,"E1"),sQuery(id+"F4.wireOp",EDGE,"E12.6.0"),sQuery(id+"F4.wireOp",EDGE,"E12.6.3")])]})});
            var Q1;
            Q1=makeQuery(id+"F5.boolean.opBoolean","COPY",EDGE,{"derivedFrom":makeQuery(id+"F5.opExtrude","SWEPT_EDGE",EDGE,{"disambiguationData":[OSD([sQuery(id+"F0.wireOp",EDGE,"E1"),sQuery(id+"F4.wireOp",EDGE,"E12.6.1"),sQuery(id+"F4.wireOp",EDGE,"E12.6.3")])]})});
            var Q2;
            Q2=makeQuery(id+"F5.boolean.opBoolean","COPY",EDGE,{"derivedFrom":makeQuery(id+"F5.opExtrude","SWEPT_EDGE",EDGE,{"disambiguationData":[OSD([sQuery(id+"F0.wireOp",EDGE,"E1"),sQuery(id+"F4.wireOp",EDGE,"E12.5.0"),sQuery(id+"F4.wireOp",EDGE,"E12.5.3")])]})});
            var Q3;
            Q3=makeQuery(id+"F5.boolean.opBoolean","COPY",EDGE,{"derivedFrom":makeQuery(id+"F5.opExtrude","SWEPT_EDGE",EDGE,{"disambiguationData":[OSD([sQuery(id+"F0.wireOp",EDGE,"E1"),sQuery(id+"F4.wireOp",EDGE,"E12.5.1"),sQuery(id+"F4.wireOp",EDGE,"E12.5.3")])]})});
            var Q4;
            Q4=makeQuery(id+"F5.boolean.opBoolean","COPY",EDGE,{"derivedFrom":makeQuery(id+"F5.opExtrude","SWEPT_EDGE",EDGE,{"disambiguationData":[OSD([sQuery(id+"F0.wireOp",EDGE,"E1"),sQuery(id+"F4.wireOp",EDGE,"E12.7.1"),sQuery(id+"F4.wireOp",EDGE,"E12.7.3")])]})});
            var Q5;
            Q5=makeQuery(id+"F5.boolean.opBoolean","COPY",EDGE,{"derivedFrom":makeQuery(id+"F5.opExtrude","SWEPT_EDGE",EDGE,{"disambiguationData":[OSD([sQuery(id+"F0.wireOp",EDGE,"E1"),sQuery(id+"F4.wireOp",EDGE,"E12.7.0"),sQuery(id+"F4.wireOp",EDGE,"E12.7.3")])]})});
            var Q6;
            Q6=makeQuery(id+"F5.boolean.opBoolean","COPY",EDGE,{"derivedFrom":makeQuery(id+"F5.opExtrude","SWEPT_EDGE",EDGE,{"disambiguationData":[OSD([sQuery(id+"F0.wireOp",EDGE,"E1"),sQuery(id+"F4.wireOp",EDGE,"E12.4.0"),sQuery(id+"F4.wireOp",EDGE,"E12.4.3")])]})});
            var Q7;
            Q7=makeQuery(id+"F5.boolean.opBoolean","COPY",EDGE,{"derivedFrom":makeQuery(id+"F5.opExtrude","SWEPT_EDGE",EDGE,{"disambiguationData":[OSD([sQuery(id+"F0.wireOp",EDGE,"E1"),sQuery(id+"F4.wireOp",EDGE,"E12.4.1"),sQuery(id+"F4.wireOp",EDGE,"E12.4.3")])]})});
            var Q8;
            Q8=makeQuery(id+"F5.boolean.opBoolean","COPY",EDGE,{"derivedFrom":makeQuery(id+"F5.opExtrude","SWEPT_EDGE",EDGE,{"disambiguationData":[OSD([sQuery(id+"F0.wireOp",EDGE,"E1"),sQuery(id+"F4.wireOp",EDGE,"E12.3.0"),sQuery(id+"F4.wireOp",EDGE,"E12.3.3")])]})});
            var Q9;
            Q9=makeQuery(id+"F5.boolean.opBoolean","COPY",EDGE,{"derivedFrom":makeQuery(id+"F5.opExtrude","SWEPT_EDGE",EDGE,{"disambiguationData":[OSD([sQuery(id+"F0.wireOp",EDGE,"E1"),sQuery(id+"F4.wireOp",EDGE,"E12.3.1"),sQuery(id+"F4.wireOp",EDGE,"E12.3.3")])]})});
            var Q10;
            Q10=makeQuery(id+"F5.boolean.opBoolean","COPY",EDGE,{"derivedFrom":makeQuery(id+"F5.opExtrude","SWEPT_EDGE",EDGE,{"disambiguationData":[OSD([sQuery(id+"F0.wireOp",EDGE,"E1"),sQuery(id+"F4.wireOp",EDGE,"E12.2.0"),sQuery(id+"F4.wireOp",EDGE,"E12.2.3")])]})});
            var Q11;
            Q11=makeQuery(id+"F5.boolean.opBoolean","COPY",EDGE,{"derivedFrom":makeQuery(id+"F5.opExtrude","SWEPT_EDGE",EDGE,{"disambiguationData":[OSD([sQuery(id+"F0.wireOp",EDGE,"E1"),sQuery(id+"F4.wireOp",EDGE,"E12.2.1"),sQuery(id+"F4.wireOp",EDGE,"E12.2.3")])]})});
            var Q12;
            Q12=makeQuery(id+"F5.boolean.opBoolean","COPY",EDGE,{"derivedFrom":makeQuery(id+"F5.opExtrude","SWEPT_EDGE",EDGE,{"disambiguationData":[OSD([sQuery(id+"F0.wireOp",EDGE,"E1"),sQuery(id+"F4.wireOp",EDGE,"E12.1.0"),sQuery(id+"F4.wireOp",EDGE,"E12.1.3")])]})});
            var Q13;
            Q13=makeQuery(id+"F5.boolean.opBoolean","COPY",EDGE,{"derivedFrom":makeQuery(id+"F5.opExtrude","SWEPT_EDGE",EDGE,{"disambiguationData":[OSD([sQuery(id+"F0.wireOp",EDGE,"E1"),sQuery(id+"F4.wireOp",EDGE,"E12.1.1"),sQuery(id+"F4.wireOp",EDGE,"E12.1.3")])]})});
            var Q14;
            Q14=makeQuery(id+"F5.boolean.opBoolean","COPY",EDGE,{"derivedFrom":makeQuery(id+"F5.opExtrude","SWEPT_EDGE",EDGE,{"disambiguationData":[OSD([sQuery(id+"F0.wireOp",EDGE,"E1"),sQuery(id+"F4.wireOp",EDGE,"E8"),sQuery(id+"F4.wireOp",EDGE,"E11")])]})});
            var Q15;
            Q15=makeQuery(id+"F5.boolean.opBoolean","COPY",EDGE,{"derivedFrom":makeQuery(id+"F5.opExtrude","SWEPT_EDGE",EDGE,{"disambiguationData":[OSD([sQuery(id+"F0.wireOp",EDGE,"E1"),sQuery(id+"F4.wireOp",EDGE,"E10"),sQuery(id+"F4.wireOp",EDGE,"E11")])]})});
            var Q16;
            Q16=makeQuery(id+"F5.boolean.opBoolean","COPY",EDGE,{"derivedFrom":makeQuery(id+"F5.opExtrude","SWEPT_EDGE",EDGE,{"disambiguationData":[OSD([sQuery(id+"F0.wireOp",EDGE,"E1"),sQuery(id+"F4.wireOp",EDGE,"E12.18.0"),sQuery(id+"F4.wireOp",EDGE,"E12.18.3")])]})});
            var Q17;
            Q17=makeQuery(id+"F5.boolean.opBoolean","COPY",EDGE,{"derivedFrom":makeQuery(id+"F5.opExtrude","SWEPT_EDGE",EDGE,{"disambiguationData":[OSD([sQuery(id+"F0.wireOp",EDGE,"E1"),sQuery(id+"F4.wireOp",EDGE,"E12.18.1"),sQuery(id+"F4.wireOp",EDGE,"E12.18.3")])]})});
            var Q18;
            Q18=makeQuery(id+"F5.boolean.opBoolean","COPY",EDGE,{"derivedFrom":makeQuery(id+"F5.opExtrude","SWEPT_EDGE",EDGE,{"disambiguationData":[OSD([sQuery(id+"F0.wireOp",EDGE,"E1"),sQuery(id+"F4.wireOp",EDGE,"E12.17.0"),sQuery(id+"F4.wireOp",EDGE,"E12.17.3")])]})});
            var Q19;
            Q19=makeQuery(id+"F5.boolean.opBoolean","COPY",EDGE,{"derivedFrom":makeQuery(id+"F5.opExtrude","SWEPT_EDGE",EDGE,{"disambiguationData":[OSD([sQuery(id+"F0.wireOp",EDGE,"E1"),sQuery(id+"F4.wireOp",EDGE,"E12.17.1"),sQuery(id+"F4.wireOp",EDGE,"E12.17.3")])]})});
            var Q20;
            Q20=makeQuery(id+"F5.boolean.opBoolean","COPY",EDGE,{"derivedFrom":makeQuery(id+"F5.opExtrude","SWEPT_EDGE",EDGE,{"disambiguationData":[OSD([sQuery(id+"F0.wireOp",EDGE,"E1"),sQuery(id+"F4.wireOp",EDGE,"E12.16.0"),sQuery(id+"F4.wireOp",EDGE,"E12.16.3")])]})});
            var Q21;
            Q21=makeQuery(id+"F5.boolean.opBoolean","COPY",EDGE,{"derivedFrom":makeQuery(id+"F5.opExtrude","SWEPT_EDGE",EDGE,{"disambiguationData":[OSD([sQuery(id+"F0.wireOp",EDGE,"E1"),sQuery(id+"F4.wireOp",EDGE,"E12.16.1"),sQuery(id+"F4.wireOp",EDGE,"E12.16.3")])]})});
            var Q22;
            Q22=makeQuery(id+"F5.boolean.opBoolean","COPY",EDGE,{"derivedFrom":makeQuery(id+"F5.opExtrude","SWEPT_EDGE",EDGE,{"disambiguationData":[OSD([sQuery(id+"F0.wireOp",EDGE,"E1"),sQuery(id+"F4.wireOp",EDGE,"E12.15.0"),sQuery(id+"F4.wireOp",EDGE,"E12.15.3")])]})});
            var Q23;
            Q23=makeQuery(id+"F5.boolean.opBoolean","COPY",EDGE,{"derivedFrom":makeQuery(id+"F5.opExtrude","SWEPT_EDGE",EDGE,{"disambiguationData":[OSD([sQuery(id+"F0.wireOp",EDGE,"E1"),sQuery(id+"F4.wireOp",EDGE,"E12.15.1"),sQuery(id+"F4.wireOp",EDGE,"E12.15.3")])]})});
            var Q24;
            Q24=makeQuery(id+"F5.boolean.opBoolean","COPY",EDGE,{"derivedFrom":makeQuery(id+"F5.opExtrude","SWEPT_EDGE",EDGE,{"disambiguationData":[OSD([sQuery(id+"F0.wireOp",EDGE,"E1"),sQuery(id+"F4.wireOp",EDGE,"E12.14.0"),sQuery(id+"F4.wireOp",EDGE,"E12.14.3")])]})});
            var Q25;
            Q25=makeQuery(id+"F5.boolean.opBoolean","COPY",EDGE,{"derivedFrom":makeQuery(id+"F5.opExtrude","SWEPT_EDGE",EDGE,{"disambiguationData":[OSD([sQuery(id+"F0.wireOp",EDGE,"E1"),sQuery(id+"F4.wireOp",EDGE,"E12.14.1"),sQuery(id+"F4.wireOp",EDGE,"E12.14.3")])]})});
            var Q26;
            Q26=makeQuery(id+"F5.boolean.opBoolean","COPY",EDGE,{"derivedFrom":makeQuery(id+"F5.opExtrude","SWEPT_EDGE",EDGE,{"disambiguationData":[OSD([sQuery(id+"F0.wireOp",EDGE,"E1"),sQuery(id+"F4.wireOp",EDGE,"E12.13.0"),sQuery(id+"F4.wireOp",EDGE,"E12.13.3")])]})});
            var Q27;
            Q27=makeQuery(id+"F5.boolean.opBoolean","COPY",EDGE,{"derivedFrom":makeQuery(id+"F5.opExtrude","SWEPT_EDGE",EDGE,{"disambiguationData":[OSD([sQuery(id+"F0.wireOp",EDGE,"E1"),sQuery(id+"F4.wireOp",EDGE,"E12.13.1"),sQuery(id+"F4.wireOp",EDGE,"E12.13.3")])]})});
            var Q28;
            Q28=makeQuery(id+"F5.boolean.opBoolean","COPY",EDGE,{"derivedFrom":makeQuery(id+"F5.opExtrude","SWEPT_EDGE",EDGE,{"disambiguationData":[OSD([sQuery(id+"F0.wireOp",EDGE,"E1"),sQuery(id+"F4.wireOp",EDGE,"E12.12.0"),sQuery(id+"F4.wireOp",EDGE,"E12.12.3")])]})});
            var Q29;
            Q29=makeQuery(id+"F5.boolean.opBoolean","COPY",EDGE,{"derivedFrom":makeQuery(id+"F5.opExtrude","SWEPT_EDGE",EDGE,{"disambiguationData":[OSD([sQuery(id+"F0.wireOp",EDGE,"E1"),sQuery(id+"F4.wireOp",EDGE,"E12.12.1"),sQuery(id+"F4.wireOp",EDGE,"E12.12.3")])]})});
            var Q30;
            Q30=makeQuery(id+"F5.boolean.opBoolean","COPY",EDGE,{"derivedFrom":makeQuery(id+"F5.opExtrude","SWEPT_EDGE",EDGE,{"disambiguationData":[OSD([sQuery(id+"F0.wireOp",EDGE,"E1"),sQuery(id+"F4.wireOp",EDGE,"E12.11.0"),sQuery(id+"F4.wireOp",EDGE,"E12.11.3")])]})});
            var Q31;
            Q31=makeQuery(id+"F5.boolean.opBoolean","COPY",EDGE,{"derivedFrom":makeQuery(id+"F5.opExtrude","SWEPT_EDGE",EDGE,{"disambiguationData":[OSD([sQuery(id+"F0.wireOp",EDGE,"E1"),sQuery(id+"F4.wireOp",EDGE,"E12.11.1"),sQuery(id+"F4.wireOp",EDGE,"E12.11.3")])]})});
            var Q32;
            Q32=makeQuery(id+"F5.boolean.opBoolean","COPY",EDGE,{"derivedFrom":makeQuery(id+"F5.opExtrude","SWEPT_EDGE",EDGE,{"disambiguationData":[OSD([sQuery(id+"F0.wireOp",EDGE,"E1"),sQuery(id+"F4.wireOp",EDGE,"E12.10.0"),sQuery(id+"F4.wireOp",EDGE,"E12.10.3")])]})});
            var Q33;
            Q33=makeQuery(id+"F5.boolean.opBoolean","COPY",EDGE,{"derivedFrom":makeQuery(id+"F5.opExtrude","SWEPT_EDGE",EDGE,{"disambiguationData":[OSD([sQuery(id+"F0.wireOp",EDGE,"E1"),sQuery(id+"F4.wireOp",EDGE,"E12.10.1"),sQuery(id+"F4.wireOp",EDGE,"E12.10.3")])]})});
            var Q34;
            Q34=makeQuery(id+"F5.boolean.opBoolean","COPY",EDGE,{"derivedFrom":makeQuery(id+"F5.opExtrude","SWEPT_EDGE",EDGE,{"disambiguationData":[OSD([sQuery(id+"F0.wireOp",EDGE,"E1"),sQuery(id+"F4.wireOp",EDGE,"E12.9.0"),sQuery(id+"F4.wireOp",EDGE,"E12.9.3")])]})});
            var Q35;
            Q35=makeQuery(id+"F5.boolean.opBoolean","COPY",EDGE,{"derivedFrom":makeQuery(id+"F5.opExtrude","SWEPT_EDGE",EDGE,{"disambiguationData":[OSD([sQuery(id+"F0.wireOp",EDGE,"E1"),sQuery(id+"F4.wireOp",EDGE,"E12.9.1"),sQuery(id+"F4.wireOp",EDGE,"E12.9.3")])]})});
            var Q36;
            Q36=makeQuery(id+"F5.boolean.opBoolean","COPY",EDGE,{"derivedFrom":makeQuery(id+"F5.opExtrude","SWEPT_EDGE",EDGE,{"disambiguationData":[OSD([sQuery(id+"F0.wireOp",EDGE,"E1"),sQuery(id+"F4.wireOp",EDGE,"E12.8.0"),sQuery(id+"F4.wireOp",EDGE,"E12.8.3")])]})});
            var Q37;
            Q37=makeQuery(id+"F5.boolean.opBoolean","COPY",EDGE,{"derivedFrom":makeQuery(id+"F5.opExtrude","SWEPT_EDGE",EDGE,{"disambiguationData":[OSD([sQuery(id+"F0.wireOp",EDGE,"E1"),sQuery(id+"F4.wireOp",EDGE,"E12.8.1"),sQuery(id+"F4.wireOp",EDGE,"E12.8.3")])]})});
            fillet(context, id + "F11", {"entities" : qUnion([Q0, Q1, Q2, Q3, Q4, Q5, Q6, Q7, Q8, Q9, Q10, Q11, Q12, Q13, Q14, Q15, Q16, Q17, Q18, Q19, Q20, Q21, Q22, Q23, Q24, Q25, Q26, Q27, Q28, Q29, Q30, Q31, Q32, Q33, Q34, Q35, Q36, Q37]), "radius" : .25 * mm, "tangentPropagation" : true, "allowEdgeOverflow" : false});
        }
    });
